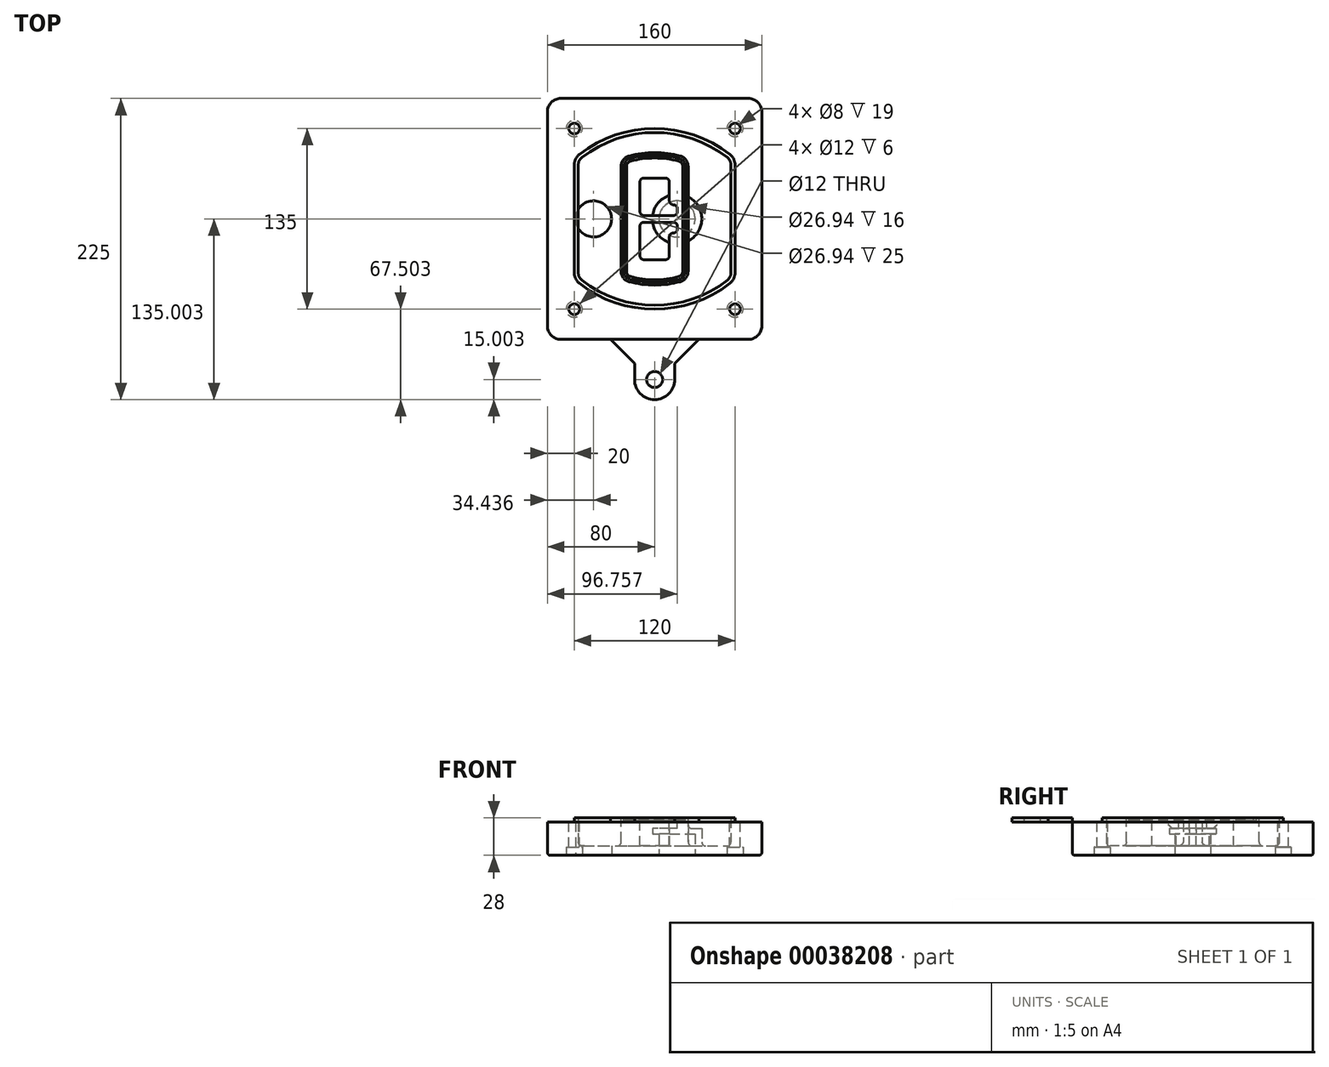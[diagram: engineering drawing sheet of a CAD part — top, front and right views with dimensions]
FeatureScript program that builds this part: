
annotation { "Feature Type Name" : "Feature", "Feature Type Description" : "" }
export const myFeature = defineFeature(function(context is Context, id is Id, definition is map)
    precondition{}
    {
        {
            var Q0;
            Q0=qCreatedBy(makeId("Top.planeOp"),FACE);
            var sketch = newSketch(context, id + "F0", { "sketchPlane" : qUnion([Q0])});
            skPoint(sketch, "E0.rect.middle", {"position": v(0, 0) * mm});
            skLineSegment(sketch, "E1.bottom", {"start": v(24.05, 28.38) * mm, "end": v(164.05, 28.38) * mm});
            skLineSegment(sketch, "E1.top", {"start": v(24.05, 208.38) * mm, "end": v(164.05, 208.38) * mm});
            skLineSegment(sketch, "E1.left", {"start": v(14.05, 38.38) * mm, "end": v(14.05, 198.38) * mm});
            skLineSegment(sketch, "E1.right", {"start": v(174.05, 38.38) * mm, "end": v(174.05, 198.38) * mm});
            skLineSegment(sketch, "E2", {"start": v(14.05, 208.38) * mm, "end": v(174.05, 28.38) * mm, "construction": true});
            skLineSegment(sketch, "E3", {"start": v(174.05, 208.38) * mm, "end": v(14.05, 28.38) * mm, "construction": true});
            skCircle(sketch, "E4", {"center": v(34.05, 185.88) * mm, "radius": 4 * mm});
            skCircle(sketch, "E5", {"center": v(154.05, 185.88) * mm, "radius": 4 * mm});
            skCircle(sketch, "E6", {"center": v(154.05, 50.88) * mm, "radius": 4 * mm});
            skCircle(sketch, "E7", {"center": v(34.05, 50.88) * mm, "radius": 4 * mm});
            skLineSegment(sketch, "E8", {"start": v(34.05, 185.88) * mm, "end": v(154.05, 185.88) * mm, "construction": true});
            skLineSegment(sketch, "E9", {"start": v(154.05, 185.88) * mm, "end": v(154.05, 50.88) * mm, "construction": true});
            skLineSegment(sketch, "E10", {"start": v(154.05, 50.88) * mm, "end": v(34.05, 50.88) * mm, "construction": true});
            skLineSegment(sketch, "E11", {"start": v(34.05, 50.88) * mm, "end": v(34.05, 185.88) * mm, "construction": true});
            skLineSegment(sketch, "E12", {"start": v(34.05, 158.68) * mm, "end": v(34.05, 78.09) * mm});
            skLineSegment(sketch, "E13", {"start": v(154.05, 158.68) * mm, "end": v(154.05, 78.09) * mm});
            skArc(sketch, "E14", {"start": v(150.2, 166.56) * mm, "mid": v(94.05, 185.88) * mm, "end": v(37.9, 166.56) * mm});
            skArc(sketch, "E15", {"start": v(37.9, 70.2) * mm, "mid": v(94.05, 50.88) * mm, "end": v(150.2, 70.2) * mm});
            skLineSegment(sketch, "E16", {"start": v(34.05, 118.38) * mm, "end": v(154.05, 118.38) * mm, "construction": true});
            skPoint(sketch, "E17.visualSharp", {"position": v(34.05, 73.38) * mm});
            skArc(sketch, "E17.filletArc", {"start": v(34.05, 78.09) * mm, "mid": v(35.06, 73.7) * mm, "end": v(37.9, 70.2) * mm});
            skPoint(sketch, "E18.visualSharp", {"position": v(34.05, 163.38) * mm});
            skArc(sketch, "E18.filletArc", {"start": v(37.9, 166.56) * mm, "mid": v(35.06, 163.06) * mm, "end": v(34.05, 158.68) * mm});
            skPoint(sketch, "E19.visualSharp", {"position": v(154.05, 163.38) * mm});
            skArc(sketch, "E19.filletArc", {"start": v(154.05, 158.68) * mm, "mid": v(153.04, 163.06) * mm, "end": v(150.2, 166.56) * mm});
            skPoint(sketch, "E20.visualSharp", {"position": v(154.05, 73.38) * mm});
            skArc(sketch, "E20.filletArc", {"start": v(150.2, 70.2) * mm, "mid": v(153.04, 73.7) * mm, "end": v(154.05, 78.09) * mm});
            skPoint(sketch, "E21.visualSharp", {"position": v(14.05, 208.38) * mm});
            skArc(sketch, "E21.filletArc", {"start": v(24.05, 208.38) * mm, "mid": v(16.98, 205.45) * mm, "end": v(14.05, 198.38) * mm});
            skPoint(sketch, "E22.visualSharp", {"position": v(174.05, 208.38) * mm});
            skArc(sketch, "E22.filletArc", {"start": v(174.05, 198.38) * mm, "mid": v(171.12, 205.45) * mm, "end": v(164.05, 208.38) * mm});
            skPoint(sketch, "E23.visualSharp", {"position": v(174.05, 28.38) * mm});
            skArc(sketch, "E23.filletArc", {"start": v(164.05, 28.38) * mm, "mid": v(171.12, 31.31) * mm, "end": v(174.05, 38.38) * mm});
            skPoint(sketch, "E24.visualSharp", {"position": v(14.05, 28.38) * mm});
            skArc(sketch, "E24.filletArc", {"start": v(14.05, 38.38) * mm, "mid": v(16.98, 31.31) * mm, "end": v(24.05, 28.38) * mm});
            skArc(sketch, "E25.0", {"start": v(151.05, 158.68) * mm, "mid": v(150.34, 161.75) * mm, "end": v(148.36, 164.2) * mm});
            skLineSegment(sketch, "E25.1", {"start": v(151.05, 158.68) * mm, "end": v(151.05, 78.09) * mm});
            skArc(sketch, "E25.2", {"start": v(148.36, 72.57) * mm, "mid": v(150.34, 75.02) * mm, "end": v(151.05, 78.09) * mm});
            skArc(sketch, "E25.3", {"start": v(39.74, 72.57) * mm, "mid": v(94.05, 53.88) * mm, "end": v(148.36, 72.57) * mm});
            skArc(sketch, "E25.4", {"start": v(37.05, 78.09) * mm, "mid": v(37.76, 75.02) * mm, "end": v(39.74, 72.57) * mm});
            skArc(sketch, "E25.5", {"start": v(148.36, 164.2) * mm, "mid": v(94.05, 182.88) * mm, "end": v(39.74, 164.2) * mm});
            skLineSegment(sketch, "E25.6", {"start": v(37.05, 158.68) * mm, "end": v(37.05, 78.09) * mm});
            skArc(sketch, "E25.7", {"start": v(39.74, 164.2) * mm, "mid": v(37.76, 161.75) * mm, "end": v(37.05, 158.68) * mm});
            skArc(sketch, "E26.0", {"start": v(35.43, 169.71) * mm, "mid": v(31.47, 164.82) * mm, "end": v(30.05, 158.68) * mm});
            skArc(sketch, "E26.1", {"start": v(152.67, 169.71) * mm, "mid": v(94.05, 189.88) * mm, "end": v(35.43, 169.71) * mm});
            skArc(sketch, "E26.2", {"start": v(158.05, 158.68) * mm, "mid": v(156.63, 164.82) * mm, "end": v(152.67, 169.71) * mm});
            skLineSegment(sketch, "E26.3", {"start": v(158.05, 158.68) * mm, "end": v(158.05, 78.09) * mm});
            skArc(sketch, "E26.4", {"start": v(152.67, 67.05) * mm, "mid": v(156.63, 71.95) * mm, "end": v(158.05, 78.09) * mm});
            skLineSegment(sketch, "E26.5", {"start": v(30.05, 158.68) * mm, "end": v(30.05, 78.09) * mm});
            skArc(sketch, "E26.6", {"start": v(35.43, 67.05) * mm, "mid": v(94.05, 46.88) * mm, "end": v(152.67, 67.05) * mm});
            skArc(sketch, "E26.7", {"start": v(30.05, 78.09) * mm, "mid": v(31.47, 71.95) * mm, "end": v(35.43, 67.05) * mm});
            skSolve(sketch);
        }
        {
            var Q0;
            Q0=makeQuery(id+"F0.imprint","IMPRINT",FACE,{"disambiguationData":[TD([[makeQuery(id+"F0.imprint","IMPRINT",EDGE,{"derivedFrom":sQuery(id+"F0.wireOp",EDGE,"E1.bottom")}),1.0]])]});
            var Q1;
            Q1=makeQuery(id+"F0.imprint","IMPRINT",FACE,{"disambiguationData":[TD([[makeQuery(id+"F0.imprint","IMPRINT",EDGE,{"derivedFrom":sQuery(id+"F0.wireOp",EDGE,"E12")}),1.0]])]});
            var Q2;
            Q2=makeQuery(id+"F0.imprint","IMPRINT",FACE,{"disambiguationData":[TD([[makeQuery(id+"F0.imprint","IMPRINT",EDGE,{"derivedFrom":sQuery(id+"F0.wireOp",EDGE,"E25.0")}),1.0]])]});
            var Q3;
            Q3=makeQuery(id+"F0.imprint","IMPRINT",FACE,{"disambiguationData":[TD([[makeQuery(id+"F0.imprint","IMPRINT",EDGE,{"derivedFrom":sQuery(id+"F0.wireOp",EDGE,"E12")}),-1.0]])]});
            extrude(context, id + "F1", {"entities" : qUnion([Q0, Q1, Q2, Q3]), "oppositeDirection" : true, "depth" : 25 * mm});
        }
        {
            var Q0;
            Q0=makeQuery(id+"F0.imprint","IMPRINT",FACE,{"disambiguationData":[TD([[makeQuery(id+"F0.imprint","IMPRINT",EDGE,{"derivedFrom":sQuery(id+"F0.wireOp",EDGE,"E12")}),1.0]])]});
            extrude(context, id + "F2", {"entities" : qUnion([Q0]), "operationType" : NewBodyOperationType.ADD, "depth" : 3 * mm});
        }
        {
            var Q0;
            Q0=makeQuery(id+"F0.imprint","IMPRINT",FACE,{"disambiguationData":[TD([[makeQuery(id+"F0.imprint","IMPRINT",EDGE,{"derivedFrom":sQuery(id+"F0.wireOp",EDGE,"E25.0")}),1.0]])]});
            extrude(context, id + "F3", {"entities" : qUnion([Q0]), "operationType" : NewBodyOperationType.REMOVE, "oppositeDirection" : true, "depth" : 18 * mm});
        }
        {
            var Q0;
            Q0=makeQuery(id+"F2.opExtrude","CAP_FACE",FACE,{"disambiguationData":[OSD([sQuery(id+"F0.wireOp",EDGE,"E12"),sQuery(id+"F0.wireOp",EDGE,"E13"),sQuery(id+"F0.wireOp",EDGE,"E14"),sQuery(id+"F0.wireOp",EDGE,"E15"),sQuery(id+"F0.wireOp",EDGE,"E17.filletArc"),sQuery(id+"F0.wireOp",EDGE,"E18.filletArc"),sQuery(id+"F0.wireOp",EDGE,"E19.filletArc"),sQuery(id+"F0.wireOp",EDGE,"E20.filletArc"),sQuery(id+"F0.wireOp",EDGE,"E25.0"),sQuery(id+"F0.wireOp",EDGE,"E25.1"),sQuery(id+"F0.wireOp",EDGE,"E25.2"),sQuery(id+"F0.wireOp",EDGE,"E25.3"),sQuery(id+"F0.wireOp",EDGE,"E25.4"),sQuery(id+"F0.wireOp",EDGE,"E25.5"),sQuery(id+"F0.wireOp",EDGE,"E25.6"),sQuery(id+"F0.wireOp",EDGE,"E25.7")])],"isStart":false});
            var sketch = newSketch(context, id + "F4", { "sketchPlane" : qUnion([Q0])});
            skArc(sketch, "E27.0", {"start": v(74.97, 71.41) * mm, "mid": v(94.05, 68.88) * mm, "end": v(113.13, 71.41) * mm});
            skArc(sketch, "E28.0", {"start": v(113.13, 165.35) * mm, "mid": v(94.05, 167.88) * mm, "end": v(74.97, 165.35) * mm});
            skLineSegment(sketch, "E29", {"start": v(69.05, 157.63) * mm, "end": v(69.05, 79.14) * mm});
            skLineSegment(sketch, "E30", {"start": v(119.05, 157.63) * mm, "end": v(119.05, 79.14) * mm});
            skLineSegment(sketch, "E31", {"start": v(69.05, 163.48) * mm, "end": v(119.05, 163.48) * mm, "construction": true});
            skLineSegment(sketch, "E32", {"start": v(69.05, 73.28) * mm, "end": v(119.05, 73.28) * mm, "construction": true});
            skPoint(sketch, "E33.visualSharp", {"position": v(69.05, 163.48) * mm});
            skArc(sketch, "E33.filletArc", {"start": v(74.97, 165.35) * mm, "mid": v(70.7, 162.5) * mm, "end": v(69.05, 157.63) * mm});
            skPoint(sketch, "E34.visualSharp", {"position": v(119.05, 163.48) * mm});
            skArc(sketch, "E34.filletArc", {"start": v(119.05, 157.63) * mm, "mid": v(117.4, 162.5) * mm, "end": v(113.13, 165.35) * mm});
            skPoint(sketch, "E35.visualSharp", {"position": v(119.05, 73.28) * mm});
            skArc(sketch, "E35.filletArc", {"start": v(113.13, 71.41) * mm, "mid": v(117.4, 74.27) * mm, "end": v(119.05, 79.14) * mm});
            skPoint(sketch, "E36.visualSharp", {"position": v(69.05, 73.28) * mm});
            skArc(sketch, "E36.filletArc", {"start": v(69.05, 79.14) * mm, "mid": v(70.7, 74.27) * mm, "end": v(74.97, 71.41) * mm});
            skArc(sketch, "E37.0", {"start": v(148.36, 164.2) * mm, "mid": v(94.05, 182.88) * mm, "end": v(39.74, 164.2) * mm});
            skArc(sketch, "E37.1", {"start": v(39.74, 164.2) * mm, "mid": v(37.76, 161.75) * mm, "end": v(37.05, 158.68) * mm});
            skLineSegment(sketch, "E37.2", {"start": v(37.05, 158.68) * mm, "end": v(37.05, 78.09) * mm});
            skArc(sketch, "E37.3", {"start": v(37.05, 78.09) * mm, "mid": v(37.76, 75.02) * mm, "end": v(39.74, 72.57) * mm});
            skArc(sketch, "E37.4", {"start": v(39.74, 72.57) * mm, "mid": v(94.05, 53.88) * mm, "end": v(148.36, 72.57) * mm});
            skArc(sketch, "E37.5", {"start": v(148.36, 72.57) * mm, "mid": v(150.34, 75.02) * mm, "end": v(151.05, 78.09) * mm});
            skLineSegment(sketch, "E37.6", {"start": v(151.05, 158.68) * mm, "end": v(151.05, 78.09) * mm});
            skArc(sketch, "E37.7", {"start": v(151.05, 158.68) * mm, "mid": v(150.34, 161.75) * mm, "end": v(148.36, 164.2) * mm});
            skLineSegment(sketch, "E38.0", {"start": v(117.05, 157.63) * mm, "end": v(117.05, 79.14) * mm});
            skArc(sketch, "E38.1", {"start": v(112.61, 73.34) * mm, "mid": v(115.81, 75.49) * mm, "end": v(117.05, 79.14) * mm});
            skArc(sketch, "E38.2", {"start": v(75.49, 73.34) * mm, "mid": v(94.05, 70.88) * mm, "end": v(112.61, 73.34) * mm});
            skArc(sketch, "E38.3", {"start": v(71.05, 79.14) * mm, "mid": v(72.29, 75.49) * mm, "end": v(75.49, 73.34) * mm});
            skLineSegment(sketch, "E38.4", {"start": v(71.05, 157.63) * mm, "end": v(71.05, 79.14) * mm});
            skArc(sketch, "E38.5", {"start": v(117.05, 157.63) * mm, "mid": v(115.81, 161.28) * mm, "end": v(112.61, 163.42) * mm});
            skArc(sketch, "E38.6", {"start": v(75.49, 163.42) * mm, "mid": v(72.29, 161.28) * mm, "end": v(71.05, 157.63) * mm});
            skArc(sketch, "E38.7", {"start": v(112.61, 163.42) * mm, "mid": v(94.05, 165.88) * mm, "end": v(75.49, 163.42) * mm});
            skArc(sketch, "E39.0", {"start": v(115.05, 157.63) * mm, "mid": v(114.23, 160.06) * mm, "end": v(112.1, 161.5) * mm});
            skLineSegment(sketch, "E39.1", {"start": v(115.05, 157.63) * mm, "end": v(115.05, 79.14) * mm});
            skArc(sketch, "E39.2", {"start": v(112.1, 75.27) * mm, "mid": v(114.23, 76.7) * mm, "end": v(115.05, 79.14) * mm});
            skArc(sketch, "E39.3", {"start": v(76, 75.27) * mm, "mid": v(94.05, 72.88) * mm, "end": v(112.1, 75.27) * mm});
            skArc(sketch, "E39.4", {"start": v(73.05, 79.14) * mm, "mid": v(73.87, 76.7) * mm, "end": v(76, 75.27) * mm});
            skArc(sketch, "E39.5", {"start": v(112.1, 161.5) * mm, "mid": v(94.05, 163.88) * mm, "end": v(76, 161.5) * mm});
            skLineSegment(sketch, "E39.6", {"start": v(73.05, 157.63) * mm, "end": v(73.05, 79.14) * mm});
            skArc(sketch, "E39.7", {"start": v(76, 161.5) * mm, "mid": v(73.87, 160.06) * mm, "end": v(73.05, 157.63) * mm});
            skLineSegment(sketch, "E40", {"start": v(69.05, 118.38) * mm, "end": v(119.05, 118.38) * mm, "construction": true});
            skLineSegment(sketch, "E41", {"start": v(83.05, 123.88) * mm, "end": v(83.05, 145.88) * mm});
            skLineSegment(sketch, "E42", {"start": v(86.05, 148.88) * mm, "end": v(102.05, 148.88) * mm});
            skLineSegment(sketch, "E43", {"start": v(105.05, 145.88) * mm, "end": v(105.05, 131.88) * mm});
            skLineSegment(sketch, "E44", {"start": v(108.05, 128.88) * mm, "end": v(108.05, 128.88) * mm});
            skLineSegment(sketch, "E45", {"start": v(111.05, 125.88) * mm, "end": v(111.05, 123.88) * mm});
            skLineSegment(sketch, "E46", {"start": v(108.05, 120.88) * mm, "end": v(86.05, 120.88) * mm});
            skPoint(sketch, "E47.visualSharp", {"position": v(83.05, 148.88) * mm});
            skArc(sketch, "E47.filletArc", {"start": v(86.05, 148.88) * mm, "mid": v(83.93, 148) * mm, "end": v(83.05, 145.88) * mm});
            skPoint(sketch, "E48.visualSharp", {"position": v(105.05, 148.88) * mm});
            skArc(sketch, "E48.filletArc", {"start": v(105.05, 145.88) * mm, "mid": v(104.17, 148) * mm, "end": v(102.05, 148.88) * mm});
            skPoint(sketch, "E49.visualSharp", {"position": v(105.05, 128.88) * mm});
            skArc(sketch, "E49.filletArc", {"start": v(105.05, 131.88) * mm, "mid": v(105.93, 129.76) * mm, "end": v(108.05, 128.88) * mm});
            skPoint(sketch, "E50.visualSharp", {"position": v(111.05, 128.88) * mm});
            skArc(sketch, "E50.filletArc", {"start": v(111.05, 125.88) * mm, "mid": v(110.17, 128) * mm, "end": v(108.05, 128.88) * mm});
            skPoint(sketch, "E51.visualSharp", {"position": v(111.05, 120.88) * mm});
            skArc(sketch, "E51.filletArc", {"start": v(108.05, 120.88) * mm, "mid": v(110.17, 121.76) * mm, "end": v(111.05, 123.88) * mm});
            skPoint(sketch, "E52.visualSharp", {"position": v(83.05, 120.88) * mm});
            skArc(sketch, "E52.filletArc", {"start": v(83.05, 123.88) * mm, "mid": v(83.93, 121.76) * mm, "end": v(86.05, 120.88) * mm});
            skLineSegment(sketch, "E53.0.MirrorCS", {"start": v(108.05, 115.88) * mm, "end": v(86.05, 115.88) * mm});
            skArc(sketch, "E54.0.MirrorCS", {"start": v(83.05, 112.88) * mm, "mid": v(83.93, 115) * mm, "end": v(86.05, 115.88) * mm});
            skLineSegment(sketch, "E55.0.MirrorCS", {"start": v(83.05, 112.88) * mm, "end": v(83.05, 90.88) * mm});
            skArc(sketch, "E56.0.MirrorCS", {"start": v(86.05, 87.88) * mm, "mid": v(83.93, 88.76) * mm, "end": v(83.05, 90.88) * mm});
            skLineSegment(sketch, "E57.0.MirrorCS", {"start": v(86.05, 87.88) * mm, "end": v(102.05, 87.88) * mm});
            skArc(sketch, "E58.0.MirrorCS", {"start": v(105.05, 90.88) * mm, "mid": v(104.17, 88.76) * mm, "end": v(102.05, 87.88) * mm});
            skLineSegment(sketch, "E59.0.MirrorCS", {"start": v(105.05, 90.88) * mm, "end": v(105.05, 104.88) * mm});
            skArc(sketch, "E60.0.MirrorCS", {"start": v(105.05, 104.88) * mm, "mid": v(105.93, 107) * mm, "end": v(108.05, 107.88) * mm});
            skArc(sketch, "E61.0.MirrorCS", {"start": v(111.05, 110.88) * mm, "mid": v(110.17, 108.76) * mm, "end": v(108.05, 107.88) * mm});
            skLineSegment(sketch, "E62.0.MirrorCS", {"start": v(111.05, 110.88) * mm, "end": v(111.05, 112.88) * mm});
            skArc(sketch, "E63.0.MirrorCS", {"start": v(108.05, 115.88) * mm, "mid": v(110.17, 115) * mm, "end": v(111.05, 112.88) * mm});
            skSolve(sketch);
        }
        {
            var Q0;
            Q0=makeQuery(id+"F4.imprint","IMPRINT",FACE,{"disambiguationData":[TD([[makeQuery(id+"F4.imprint","IMPRINT",EDGE,{"derivedFrom":sQuery(id+"F4.wireOp",EDGE,"E27.0")}),1.0]])]});
            var Q1;
            Q1=makeQuery(id+"F4.imprint","IMPRINT",FACE,{"disambiguationData":[TD([[makeQuery(id+"F4.imprint","IMPRINT",EDGE,{"derivedFrom":sQuery(id+"F4.wireOp",EDGE,"E38.0")}),-1.0]])]});
            var Q2;
            Q2=makeQuery(id+"F4.imprint","IMPRINT",FACE,{"disambiguationData":[TD([[makeQuery(id+"F4.imprint","IMPRINT",EDGE,{"derivedFrom":sQuery(id+"F4.wireOp",EDGE,"E39.0")}),1.0]])]});
            extrude(context, id + "F5", {"entities" : qUnion([Q0, Q1, Q2]), "operationType" : NewBodyOperationType.ADD, "endBound" : BoundingType.UP_TO_NEXT, "oppositeDirection" : true, "depth" : 25 * mm});
        }
        {
            var Q0;
            Q0=makeQuery(id+"F4.imprint","IMPRINT",FACE,{"disambiguationData":[TD([[makeQuery(id+"F4.imprint","IMPRINT",EDGE,{"derivedFrom":sQuery(id+"F4.wireOp",EDGE,"E38.0")}),-1.0]])]});
            extrude(context, id + "F6", {"entities" : qUnion([Q0]), "operationType" : NewBodyOperationType.REMOVE, "oppositeDirection" : true, "depth" : 2 * mm});
        }
        {
            var Q0;
            Q0=makeQuery(id+"F1.opExtrude","CAP_FACE",FACE,{"disambiguationData":[OSD([sQuery(id+"F0.wireOp",EDGE,"E1.bottom"),sQuery(id+"F0.wireOp",EDGE,"E1.top"),sQuery(id+"F0.wireOp",EDGE,"E1.left"),sQuery(id+"F0.wireOp",EDGE,"E1.right"),sQuery(id+"F0.wireOp",EDGE,"E4"),sQuery(id+"F0.wireOp",EDGE,"E5"),sQuery(id+"F0.wireOp",EDGE,"E6"),sQuery(id+"F0.wireOp",EDGE,"E7"),sQuery(id+"F0.wireOp",EDGE,"E21.filletArc"),sQuery(id+"F0.wireOp",EDGE,"E22.filletArc"),sQuery(id+"F0.wireOp",EDGE,"E23.filletArc"),sQuery(id+"F0.wireOp",EDGE,"E24.filletArc")])],"isStart":false});
            var sketch = newSketch(context, id + "F7", { "sketchPlane" : qUnion([Q0])});
            skCircle(sketch, "E64", {"center": v(110.8, -118.38) * mm, "radius": 13.47 * mm});
            skCircle(sketch, "E65", {"center": v(48.49, -118.38) * mm, "radius": 13.47 * mm});
            skLineSegment(sketch, "E66", {"start": v(174.05, -118.38) * mm, "end": v(14.05, -118.38) * mm});
            skCircle(sketch, "E67", {"center": v(110.8, -118.38) * mm, "radius": 18.47 * mm});
            skCircle(sketch, "E68", {"center": v(154.05, -185.88) * mm, "radius": 6 * mm});
            skCircle(sketch, "E69", {"center": v(34.05, -185.88) * mm, "radius": 6 * mm});
            skCircle(sketch, "E70", {"center": v(34.05, -50.88) * mm, "radius": 6 * mm});
            skCircle(sketch, "E71", {"center": v(154.05, -50.88) * mm, "radius": 6 * mm});
            skSolve(sketch);
        }
        {
            var Q0;
            {var subQ1=sQuery(id+"F7.wireOp",EDGE,"E66");var subQ4=sQuery(id+"F7.wireOp",EDGE,"E64");var subQ6=makeQuery(id+"F7.imprint","INTERSECT",VERTEX,{"disambiguationData":[OD(0.0)],"derivedFrom":[subQ4,subQ1]});Q0=makeQuery(id+"F7.imprint","IMPRINT",FACE,{"disambiguationData":[TD([[makeQuery(id+"F7.imprint","IMPRINT",EDGE,{"disambiguationData":[TD([[subQ6,-1.0]])],"derivedFrom":subQ4}),-1.0]])]});}
            var Q1;
            {var subQ0=sQuery(id+"F7.wireOp",EDGE,"E66");var subQ1=sQuery(id+"F7.wireOp",EDGE,"E64");var subQ3=makeQuery(id+"F7.imprint","INTERSECT",VERTEX,{"disambiguationData":[OD(0.0)],"derivedFrom":[subQ1,subQ0]});Q1=makeQuery(id+"F7.imprint","IMPRINT",FACE,{"disambiguationData":[TD([[makeQuery(id+"F7.imprint","IMPRINT",EDGE,{"disambiguationData":[TD([[subQ3,-1.0]])],"derivedFrom":subQ1}),1.0]])]});}
            var Q2;
            {var subQ0=sQuery(id+"F7.wireOp",EDGE,"E66");var subQ1=sQuery(id+"F7.wireOp",EDGE,"E64");var subQ3=makeQuery(id+"F7.imprint","INTERSECT",VERTEX,{"disambiguationData":[OD(0.0)],"derivedFrom":[subQ1,subQ0]});Q2=makeQuery(id+"F7.imprint","IMPRINT",FACE,{"disambiguationData":[TD([[makeQuery(id+"F7.imprint","IMPRINT",EDGE,{"disambiguationData":[TD([[subQ3,1.0]])],"derivedFrom":subQ1}),1.0]])]});}
            var Q3;
            {var subQ1=sQuery(id+"F7.wireOp",EDGE,"E66");var subQ4=sQuery(id+"F7.wireOp",EDGE,"E64");var subQ6=makeQuery(id+"F7.imprint","INTERSECT",VERTEX,{"disambiguationData":[OD(0.0)],"derivedFrom":[subQ4,subQ1]});Q3=makeQuery(id+"F7.imprint","IMPRINT",FACE,{"disambiguationData":[TD([[makeQuery(id+"F7.imprint","IMPRINT",EDGE,{"disambiguationData":[TD([[subQ6,1.0]])],"derivedFrom":subQ4}),-1.0]])]});}
            extrude(context, id + "F8", {"entities" : qUnion([Q0, Q1, Q2, Q3]), "operationType" : NewBodyOperationType.ADD, "oppositeDirection" : true, "depth" : 20 * mm});
        }
        {
            var Q0;
            {var subQ0=sQuery(id+"F7.wireOp",EDGE,"E66");var subQ1=sQuery(id+"F7.wireOp",EDGE,"E64");var subQ3=makeQuery(id+"F7.imprint","INTERSECT",VERTEX,{"disambiguationData":[OD(0.0)],"derivedFrom":[subQ1,subQ0]});Q0=makeQuery(id+"F7.imprint","IMPRINT",FACE,{"disambiguationData":[TD([[makeQuery(id+"F7.imprint","IMPRINT",EDGE,{"disambiguationData":[TD([[subQ3,-1.0]])],"derivedFrom":subQ1}),1.0]])]});}
            var Q1;
            {var subQ0=sQuery(id+"F7.wireOp",EDGE,"E66");var subQ1=sQuery(id+"F7.wireOp",EDGE,"E64");var subQ3=makeQuery(id+"F7.imprint","INTERSECT",VERTEX,{"disambiguationData":[OD(0.0)],"derivedFrom":[subQ1,subQ0]});Q1=makeQuery(id+"F7.imprint","IMPRINT",FACE,{"disambiguationData":[TD([[makeQuery(id+"F7.imprint","IMPRINT",EDGE,{"disambiguationData":[TD([[subQ3,1.0]])],"derivedFrom":subQ1}),1.0]])]});}
            extrude(context, id + "F9", {"entities" : qUnion([Q0, Q1]), "operationType" : NewBodyOperationType.REMOVE, "oppositeDirection" : true, "depth" : 16 * mm});
        }
        {
            var Q0;
            {var subQ0=sQuery(id+"F7.wireOp",EDGE,"E66");var subQ1=sQuery(id+"F7.wireOp",EDGE,"E65");var subQ3=makeQuery(id+"F7.imprint","INTERSECT",VERTEX,{"disambiguationData":[OD(0.0)],"derivedFrom":[subQ1,subQ0]});Q0=makeQuery(id+"F7.imprint","IMPRINT",FACE,{"disambiguationData":[TD([[makeQuery(id+"F7.imprint","IMPRINT",EDGE,{"disambiguationData":[TD([[subQ3,-1.0]])],"derivedFrom":subQ1}),1.0]])]});}
            var Q1;
            {var subQ0=sQuery(id+"F7.wireOp",EDGE,"E66");var subQ1=sQuery(id+"F7.wireOp",EDGE,"E65");var subQ3=makeQuery(id+"F7.imprint","INTERSECT",VERTEX,{"disambiguationData":[OD(0.0)],"derivedFrom":[subQ1,subQ0]});Q1=makeQuery(id+"F7.imprint","IMPRINT",FACE,{"disambiguationData":[TD([[makeQuery(id+"F7.imprint","IMPRINT",EDGE,{"disambiguationData":[TD([[subQ3,1.0]])],"derivedFrom":subQ1}),1.0]])]});}
            extrude(context, id + "F10", {"entities" : qUnion([Q0, Q1]), "operationType" : NewBodyOperationType.REMOVE, "oppositeDirection" : true, "depth" : 25 * mm});
        }
        {
            var Q0;
            Q0=makeQuery(id+"F7.imprint","IMPRINT",FACE,{"disambiguationData":[TD([[makeQuery(id+"F7.imprint","IMPRINT",EDGE,{"derivedFrom":sQuery(id+"F7.wireOp",EDGE,"E68")}),1.0]])]});
            var Q1;
            Q1=makeQuery(id+"F7.imprint","IMPRINT",FACE,{"disambiguationData":[TD([[makeQuery(id+"F7.imprint","IMPRINT",EDGE,{"derivedFrom":makeQuery(id+"F1.opExtrude","CAP_EDGE",EDGE,{"disambiguationData":[OSD([sQuery(id+"F0.wireOp",EDGE,"E5")])],"isStart":false})}),-1.0]])]});
            var Q2;
            Q2=makeQuery(id+"F7.imprint","IMPRINT",FACE,{"disambiguationData":[TD([[makeQuery(id+"F7.imprint","IMPRINT",EDGE,{"derivedFrom":sQuery(id+"F7.wireOp",EDGE,"E69")}),1.0]])]});
            var Q3;
            Q3=makeQuery(id+"F7.imprint","IMPRINT",FACE,{"disambiguationData":[TD([[makeQuery(id+"F7.imprint","IMPRINT",EDGE,{"derivedFrom":makeQuery(id+"F1.opExtrude","CAP_EDGE",EDGE,{"disambiguationData":[OSD([sQuery(id+"F0.wireOp",EDGE,"E4")])],"isStart":false})}),-1.0]])]});
            var Q4;
            Q4=makeQuery(id+"F7.imprint","IMPRINT",FACE,{"disambiguationData":[TD([[makeQuery(id+"F7.imprint","IMPRINT",EDGE,{"derivedFrom":sQuery(id+"F7.wireOp",EDGE,"E70")}),1.0]])]});
            var Q5;
            Q5=makeQuery(id+"F7.imprint","IMPRINT",FACE,{"disambiguationData":[TD([[makeQuery(id+"F7.imprint","IMPRINT",EDGE,{"derivedFrom":makeQuery(id+"F1.opExtrude","CAP_EDGE",EDGE,{"disambiguationData":[OSD([sQuery(id+"F0.wireOp",EDGE,"E7")])],"isStart":false})}),-1.0]])]});
            var Q6;
            Q6=makeQuery(id+"F7.imprint","IMPRINT",FACE,{"disambiguationData":[TD([[makeQuery(id+"F7.imprint","IMPRINT",EDGE,{"derivedFrom":sQuery(id+"F7.wireOp",EDGE,"E71")}),1.0]])]});
            var Q7;
            Q7=makeQuery(id+"F7.imprint","IMPRINT",FACE,{"disambiguationData":[TD([[makeQuery(id+"F7.imprint","IMPRINT",EDGE,{"derivedFrom":makeQuery(id+"F1.opExtrude","CAP_EDGE",EDGE,{"disambiguationData":[OSD([sQuery(id+"F0.wireOp",EDGE,"E6")])],"isStart":false})}),-1.0]])]});
            extrude(context, id + "F11", {"entities" : qUnion([Q0, Q1, Q2, Q3, Q4, Q5, Q6, Q7]), "operationType" : NewBodyOperationType.REMOVE, "oppositeDirection" : true, "depth" : 6 * mm});
        }
        {
            var Q0;
            Q0=makeQuery(id+"F9.boolean.opBoolean","COPY",FACE,{"derivedFrom":makeQuery(id+"F9.opExtrude","CAP_FACE",FACE,{"disambiguationData":[OSD([sQuery(id+"F7.wireOp",EDGE,"E64")])],"isStart":false})});
            var sketch = newSketch(context, id + "F12", { "sketchPlane" : qUnion([Q0])});
            skArc(sketch, "E72.0", {"start": v(105.05, -100.83) * mm, "mid": v(96.62, -106.56) * mm, "end": v(92.5, -115.88) * mm});
            skArc(sketch, "E72.1", {"start": v(92.5, -120.88) * mm, "mid": v(96.62, -130.2) * mm, "end": v(105.05, -135.93) * mm});
            skLineSegment(sketch, "E73", {"start": v(92.5, -120.88) * mm, "end": v(108.05, -120.88) * mm});
            skLineSegment(sketch, "E74.0", {"start": v(108.05, -115.88) * mm, "end": v(92.5, -115.88) * mm});
            skArc(sketch, "E74.1", {"start": v(108.05, -115.88) * mm, "mid": v(110.17, -115) * mm, "end": v(111.05, -112.88) * mm});
            skLineSegment(sketch, "E74.2", {"start": v(111.05, -110.88) * mm, "end": v(111.05, -112.88) * mm});
            skArc(sketch, "E74.3", {"start": v(111.05, -110.88) * mm, "mid": v(110.17, -108.76) * mm, "end": v(108.05, -107.88) * mm});
            skArc(sketch, "E74.4", {"start": v(105.05, -104.88) * mm, "mid": v(105.93, -107) * mm, "end": v(108.05, -107.88) * mm});
            skLineSegment(sketch, "E74.5", {"start": v(105.05, -100.83) * mm, "end": v(105.05, -104.88) * mm});
            skLineSegment(sketch, "E74.7", {"start": v(108.05, -120.88) * mm, "end": v(92.5, -120.88) * mm});
            skArc(sketch, "E74.8", {"start": v(108.05, -120.88) * mm, "mid": v(110.17, -121.76) * mm, "end": v(111.05, -123.88) * mm});
            skLineSegment(sketch, "E74.9", {"start": v(111.05, -125.88) * mm, "end": v(111.05, -123.88) * mm});
            skArc(sketch, "E74.10", {"start": v(111.05, -125.88) * mm, "mid": v(110.17, -128) * mm, "end": v(108.05, -128.88) * mm});
            skArc(sketch, "E74.11", {"start": v(105.05, -131.88) * mm, "mid": v(105.93, -129.76) * mm, "end": v(108.05, -128.88) * mm});
            skLineSegment(sketch, "E74.12", {"start": v(105.05, -135.93) * mm, "end": v(105.05, -131.88) * mm});
            skPoint(sketch, "E75.orphan", {"position": v(105.05, -145.88) * mm});
            skPoint(sketch, "E76.orphan", {"position": v(86.05, -120.88) * mm});
            skPoint(sketch, "E77.orphan", {"position": v(86.05, -115.88) * mm});
            skPoint(sketch, "E78.orphan", {"position": v(105.05, -90.88) * mm});
            skSolve(sketch);
        }
        {
            var Q0;
            {var subQ7=sQuery(id+"F12.wireOp",EDGE,"E72.0");var subQ14=sQuery(id+"F12.wireOp",EDGE,"E72.1");var subQ16=sQuery(id+"F12.wireOp",EDGE,"E74.1");var subQ18=sQuery(id+"F12.wireOp",EDGE,"E74.8");Q0=qUnion([makeQuery(id+"F12.imprint","IMPRINT",FACE,{"disambiguationData":[TD([[makeQuery(id+"F12.imprint","IMPRINT",EDGE,{"derivedFrom":subQ7}),1.0]])]}),makeQuery(id+"F12.imprint","IMPRINT",FACE,{"disambiguationData":[TD([[makeQuery(id+"F12.imprint","IMPRINT",EDGE,{"derivedFrom":subQ14}),1.0]])]}),makeQuery(id+"F12.imprint","IMPRINT",FACE,{"disambiguationData":[TD([[makeQuery(id+"F12.imprint","IMPRINT",EDGE,{"derivedFrom":subQ16}),1.0]])]}),makeQuery(id+"F12.imprint","IMPRINT",FACE,{"disambiguationData":[TD([[makeQuery(id+"F12.imprint","IMPRINT",EDGE,{"derivedFrom":subQ18}),-1.0]])]})]);}
            var Q1;
            Q1=makeQuery(id+"F5.boolean.opBoolean","SPLIT",FACE,{"disambiguationData":[TD([makeQuery(id+"F5.opExtrude","SWEPT_FACE",FACE,{"disambiguationData":[OSD([sQuery(id+"F4.wireOp",EDGE,"E41")])]})])],"derivedFrom":makeQuery(id+"F3.boolean.opBoolean","COPY",FACE,{"derivedFrom":makeQuery(id+"F3.opExtrude","CAP_FACE",FACE,{"disambiguationData":[OSD([sQuery(id+"F0.wireOp",EDGE,"E25.0"),sQuery(id+"F0.wireOp",EDGE,"E25.1"),sQuery(id+"F0.wireOp",EDGE,"E25.2"),sQuery(id+"F0.wireOp",EDGE,"E25.3"),sQuery(id+"F0.wireOp",EDGE,"E25.4"),sQuery(id+"F0.wireOp",EDGE,"E25.5"),sQuery(id+"F0.wireOp",EDGE,"E25.6"),sQuery(id+"F0.wireOp",EDGE,"E25.7")])],"isStart":false})})});
            extrude(context, id + "F13", {"entities" : qUnion([Q0]), "operationType" : NewBodyOperationType.REMOVE, "endBound" : BoundingType.UP_TO_SURFACE, "endBoundEntityFace" : qUnion([Q1]), "depth" : 25 * mm});
        }
        {
            var Q0;
            Q0=makeQuery(id+"F3.boolean.opBoolean","COPY",EDGE,{"derivedFrom":makeQuery(id+"F3.opExtrude","CAP_EDGE",EDGE,{"disambiguationData":[OSD([sQuery(id+"F0.wireOp",EDGE,"E25.6")])],"isStart":false})});
            var Q1;
            Q1=makeQuery(id+"F8.boolean.opBoolean","INTERSECT",EDGE,{"derivedFrom":[makeQuery(id+"F5.opExtrude","SWEPT_FACE",FACE,{"disambiguationData":[OSD([sQuery(id+"F4.wireOp",EDGE,"E30")])]}),makeQuery(id+"F8.opExtrude","CAP_FACE",FACE,{"disambiguationData":[OSD([sQuery(id+"F7.wireOp",EDGE,"E67")])],"isStart":false})]});
            var Q2;
            Q2=makeQuery(id+"F8.boolean.opBoolean","INTERSECT",EDGE,{"disambiguationData":[OD(1.0)],"derivedFrom":[makeQuery(id+"F5.opExtrude","SWEPT_FACE",FACE,{"disambiguationData":[OSD([sQuery(id+"F4.wireOp",EDGE,"E30")])]}),makeQuery(id+"F8.opExtrude","SWEPT_FACE",FACE,{"disambiguationData":[OSD([sQuery(id+"F7.wireOp",EDGE,"E67")])]})]});
            var Q3;
            {var subQ0=sQuery(id+"F4.wireOp",EDGE,"E30");Q3=makeQuery(id+"F8.boolean.opBoolean","SPLIT",EDGE,{"disambiguationData":[TD([makeQuery(id+"F5.opExtrude","SWEPT_FACE",FACE,{"disambiguationData":[OSD([sQuery(id+"F4.wireOp",EDGE,"E35.filletArc")])]})])],"derivedFrom":makeQuery(id+"F5.opExtrude","CAP_EDGE",EDGE,{"disambiguationData":[OSD([subQ0])],"isStart":false})});}
            var Q4;
            {var subQ0=sQuery(id+"F0.wireOp",EDGE,"E25.7");var subQ1=sQuery(id+"F0.wireOp",EDGE,"E25.1");var subQ2=sQuery(id+"F0.wireOp",EDGE,"E25.6");var subQ3=sQuery(id+"F0.wireOp",EDGE,"E25.5");var subQ4=sQuery(id+"F0.wireOp",EDGE,"E25.4");var subQ5=sQuery(id+"F0.wireOp",EDGE,"E25.0");var subQ6=sQuery(id+"F0.wireOp",EDGE,"E25.2");var subQ7=sQuery(id+"F0.wireOp",EDGE,"E25.3");Q4=makeQuery(id+"F8.boolean.opBoolean","INTERSECT",EDGE,{"derivedFrom":[makeQuery(id+"F5.boolean.opBoolean","SPLIT",FACE,{"disambiguationData":[TD([makeQuery(id+"F2.opExtrude","SWEPT_FACE",FACE,{"disambiguationData":[OSD([subQ5])]})])],"derivedFrom":makeQuery(id+"F3.boolean.opBoolean","COPY",FACE,{"derivedFrom":makeQuery(id+"F3.opExtrude","CAP_FACE",FACE,{"disambiguationData":[OSD([subQ5,subQ1,subQ6,subQ7,subQ4,subQ3,subQ2,subQ0])],"isStart":false})})}),makeQuery(id+"F8.opExtrude","SWEPT_FACE",FACE,{"disambiguationData":[OSD([sQuery(id+"F7.wireOp",EDGE,"E67")])]})]});}
            var Q5;
            Q5=makeQuery(id+"F8.boolean.opBoolean","INTERSECT",EDGE,{"disambiguationData":[OD(0.0)],"derivedFrom":[makeQuery(id+"F5.opExtrude","SWEPT_FACE",FACE,{"disambiguationData":[OSD([sQuery(id+"F4.wireOp",EDGE,"E30")])]}),makeQuery(id+"F8.opExtrude","SWEPT_FACE",FACE,{"disambiguationData":[OSD([sQuery(id+"F7.wireOp",EDGE,"E67")])]})]});
            fillet(context, id + "F14", {"entities" : qUnion([Q0, Q1, Q2, Q3, Q4, Q5]), "radius" : 3 * mm, "tangentPropagation" : true, "allowEdgeOverflow" : false});
        }
        {
            var Q0;
            Q0=makeQuery(id+"F1.opExtrude","CAP_EDGE",EDGE,{"disambiguationData":[OSD([sQuery(id+"F0.wireOp",EDGE,"E1.bottom")])],"isStart":false});
            fillet(context, id + "F15", {"entities" : qUnion([Q0]), "radius" : 2 * mm, "tangentPropagation" : true, "allowEdgeOverflow" : false});
        }
        {
            var Q0;
            {var subQ0=sQuery(id+"F0.wireOp",EDGE,"E1.bottom");var subQ1=sQuery(id+"F0.wireOp",EDGE,"E1.top");var subQ2=sQuery(id+"F0.wireOp",EDGE,"E1.left");var subQ3=sQuery(id+"F0.wireOp",EDGE,"E1.right");var subQ4=sQuery(id+"F0.wireOp",EDGE,"E4");var subQ5=sQuery(id+"F0.wireOp",EDGE,"E5");var subQ6=sQuery(id+"F0.wireOp",EDGE,"E6");var subQ7=sQuery(id+"F0.wireOp",EDGE,"E7");var subQ8=sQuery(id+"F0.wireOp",EDGE,"E21.filletArc");var subQ9=sQuery(id+"F0.wireOp",EDGE,"E22.filletArc");var subQ10=sQuery(id+"F0.wireOp",EDGE,"E23.filletArc");var subQ11=sQuery(id+"F0.wireOp",EDGE,"E24.filletArc");Q0=makeQuery(id+"F2.boolean.opBoolean","SPLIT",FACE,{"disambiguationData":[TD([makeQuery(id+"F1.opExtrude","SWEPT_FACE",FACE,{"disambiguationData":[OSD([subQ0])]})])],"derivedFrom":makeQuery(id+"F1.opExtrude","CAP_FACE",FACE,{"disambiguationData":[OSD([subQ0,subQ1,subQ2,subQ3,subQ4,subQ5,subQ6,subQ7,subQ8,subQ9,subQ10,subQ11])],"isStart":true})});}
            var sketch = newSketch(context, id + "F16", { "sketchPlane" : qUnion([Q0])});
            skLineSegment(sketch, "E79.0", {"start": v(24.05, 208.38) * mm, "end": v(164.05, 208.38) * mm});
            skArc(sketch, "E79.1", {"start": v(24.05, 208.38) * mm, "mid": v(16.98, 205.45) * mm, "end": v(14.05, 198.38) * mm});
            skLineSegment(sketch, "E79.2", {"start": v(14.05, 38.38) * mm, "end": v(14.05, 198.38) * mm});
            skArc(sketch, "E79.3", {"start": v(14.05, 38.38) * mm, "mid": v(16.98, 31.31) * mm, "end": v(24.05, 28.38) * mm});
            skLineSegment(sketch, "E79.4", {"start": v(24.05, 28.38) * mm, "end": v(164.05, 28.38) * mm});
            skArc(sketch, "E79.5", {"start": v(164.05, 28.38) * mm, "mid": v(171.12, 31.31) * mm, "end": v(174.05, 38.38) * mm});
            skLineSegment(sketch, "E79.6", {"start": v(174.05, 38.38) * mm, "end": v(174.05, 198.38) * mm});
            skArc(sketch, "E79.7", {"start": v(174.05, 198.38) * mm, "mid": v(171.12, 205.45) * mm, "end": v(164.05, 208.38) * mm});
            skCircle(sketch, "E79.8", {"center": v(154.05, 185.88) * mm, "radius": 4 * mm});
            skCircle(sketch, "E79.9", {"center": v(34.05, 185.88) * mm, "radius": 4 * mm});
            skArc(sketch, "E79.10", {"start": v(150.2, 166.56) * mm, "mid": v(94.05, 185.88) * mm, "end": v(37.9, 166.56) * mm});
            skArc(sketch, "E79.11", {"start": v(37.9, 166.56) * mm, "mid": v(35.06, 163.06) * mm, "end": v(34.05, 158.68) * mm});
            skLineSegment(sketch, "E79.12", {"start": v(34.05, 158.68) * mm, "end": v(34.05, 78.09) * mm});
            skArc(sketch, "E79.13", {"start": v(154.05, 158.68) * mm, "mid": v(153.04, 163.06) * mm, "end": v(150.2, 166.56) * mm});
            skLineSegment(sketch, "E79.14", {"start": v(154.05, 158.68) * mm, "end": v(154.05, 78.09) * mm});
            skArc(sketch, "E79.15", {"start": v(150.2, 70.2) * mm, "mid": v(153.04, 73.7) * mm, "end": v(154.05, 78.09) * mm});
            skArc(sketch, "E79.16", {"start": v(37.9, 70.2) * mm, "mid": v(94.05, 50.88) * mm, "end": v(150.2, 70.2) * mm});
            skCircle(sketch, "E79.17", {"center": v(154.05, 50.88) * mm, "radius": 4 * mm});
            skCircle(sketch, "E79.18", {"center": v(34.05, 50.88) * mm, "radius": 4 * mm});
            skArc(sketch, "E79.19", {"start": v(34.05, 78.09) * mm, "mid": v(35.06, 73.7) * mm, "end": v(37.9, 70.2) * mm});
            skArc(sketch, "E80.1", {"start": v(24.05, 188.38) * mm, "mid": v(31.12, 205.45) * mm, "end": v(14.05, 198.38) * mm});
            skLineSegment(sketch, "E81", {"start": v(94.05, 208.38) * mm, "end": v(94.05, 238.38) * mm, "construction": true});
            skLineSegment(sketch, "E82", {"start": v(79.05, 238.38) * mm, "end": v(79.05, 226.38) * mm});
            skLineSegment(sketch, "E83", {"start": v(109.05, 226.38) * mm, "end": v(109.05, 238.38) * mm});
            skArc(sketch, "E84", {"start": v(109.05, 238.38) * mm, "mid": v(94.05, 253.38) * mm, "end": v(79.05, 238.38) * mm});
            skCircle(sketch, "E85", {"center": v(94.05, 238.38) * mm, "radius": 6 * mm});
            skLineSegment(sketch, "E86", {"start": v(61.05, 208.38) * mm, "end": v(79.05, 226.38) * mm});
            skLineSegment(sketch, "E87", {"start": v(109.05, 226.38) * mm, "end": v(127.05, 208.38) * mm});
            skLineSegment(sketch, "E88", {"start": v(14.05, 118.38) * mm, "end": v(174.05, 118.38) * mm, "construction": true});
            skLineSegment(sketch, "E89.MirrorCS", {"start": v(79.05, 226.38) * mm, "end": v(61.05, 208.38) * mm});
            skLineSegment(sketch, "E90.MirrorCS", {"start": v(79.05, 226.38) * mm, "end": v(79.05, 238.38) * mm});
            skArc(sketch, "E91.MirrorCS", {"start": v(79.05, 238.38) * mm, "mid": v(94.05, 253.38) * mm, "end": v(109.05, 238.38) * mm});
            skLineSegment(sketch, "E92.MirrorCS", {"start": v(109.05, 238.38) * mm, "end": v(109.05, 226.38) * mm});
            skLineSegment(sketch, "E93.MirrorCS", {"start": v(127.05, 208.38) * mm, "end": v(109.05, 226.38) * mm});
            skLineSegment(sketch, "E94.MirrorCS", {"start": v(174.05, 118.38) * mm, "end": v(14.05, 118.38) * mm, "construction": true});
            skLineSegment(sketch, "E95.MirrorCS", {"start": v(164.05, 28.38) * mm, "end": v(24.05, 28.38) * mm});
            skCircle(sketch, "E96.MirrorC", {"center": v(94.05, -1.62) * mm, "radius": 6 * mm});
            skLineSegment(sketch, "E97.MirrorCS", {"start": v(79.05, -1.62) * mm, "end": v(79.05, 10.38) * mm});
            skLineSegment(sketch, "E98.MirrorCS", {"start": v(79.05, 10.38) * mm, "end": v(79.05, -1.62) * mm});
            skLineSegment(sketch, "E99.MirrorCS", {"start": v(61.05, 28.38) * mm, "end": v(79.05, 10.38) * mm});
            skLineSegment(sketch, "E100.MirrorCS", {"start": v(109.05, 10.38) * mm, "end": v(109.05, -1.62) * mm});
            skLineSegment(sketch, "E101.MirrorCS", {"start": v(79.05, 10.38) * mm, "end": v(61.05, 28.38) * mm});
            skLineSegment(sketch, "E102.MirrorCS", {"start": v(109.05, -1.62) * mm, "end": v(109.05, 10.38) * mm});
            skLineSegment(sketch, "E103.MirrorCS", {"start": v(127.05, 28.38) * mm, "end": v(109.05, 10.38) * mm});
            skArc(sketch, "E104.MirrorCS", {"start": v(109.05, -1.62) * mm, "mid": v(94.05, -16.62) * mm, "end": v(79.05, -1.62) * mm});
            skArc(sketch, "E105.MirrorCS", {"start": v(79.05, -1.62) * mm, "mid": v(94.05, -16.62) * mm, "end": v(109.05, -1.62) * mm});
            skLineSegment(sketch, "E106.MirrorCS", {"start": v(109.05, 10.38) * mm, "end": v(127.05, 28.38) * mm});
            skArc(sketch, "E107.MirrorCS", {"start": v(174.05, 38.38) * mm, "mid": v(171.12, 31.31) * mm, "end": v(164.05, 28.38) * mm});
            skArc(sketch, "E108.MirrorCS", {"start": v(154.05, 78.09) * mm, "mid": v(153.04, 73.7) * mm, "end": v(150.2, 70.2) * mm});
            skLineSegment(sketch, "E109.MirrorCS", {"start": v(94.05, 28.38) * mm, "end": v(94.05, -1.62) * mm});
            skSolve(sketch);
        }
        {
            var Q0;
            Q0=makeQuery(id+"F16.imprint","IMPRINT",FACE,{"disambiguationData":[TD([[makeQuery(id+"F16.imprint","IMPRINT",EDGE,{"derivedFrom":sQuery(id+"F16.wireOp",EDGE,"E91.MirrorCS")}),-1.0]])]});
            var Q1;
            {var subQ3=sQuery(id+"F16.wireOp",EDGE,"E99.MirrorCS");Q1=makeQuery(id+"F16.imprint","IMPRINT",FACE,{"disambiguationData":[TD([[makeQuery(id+"F16.imprint","IMPRINT",EDGE,{"derivedFrom":subQ3}),1.0]])]});}
            var Q2;
            {var subQ5=sQuery(id+"F16.wireOp",EDGE,"E80.1");Q2=makeQuery(id+"F16.imprint","IMPRINT",FACE,{"disambiguationData":[TD([[makeQuery(id+"F16.imprint","IMPRINT",EDGE,{"derivedFrom":subQ5}),1.0]])]});}
            var Q3;
            {var subQ0=sQuery(id+"F4.wireOp",EDGE,"E36.filletArc");var subQ1=sQuery(id+"F4.wireOp",EDGE,"E35.filletArc");var subQ2=sQuery(id+"F4.wireOp",EDGE,"E34.filletArc");var subQ3=sQuery(id+"F4.wireOp",EDGE,"E33.filletArc");var subQ4=sQuery(id+"F4.wireOp",EDGE,"E27.0");var subQ5=sQuery(id+"F4.wireOp",EDGE,"E30");var subQ6=sQuery(id+"F4.wireOp",EDGE,"E28.0");var subQ7=sQuery(id+"F4.wireOp",EDGE,"E29");Q3=makeQuery(id+"F6.boolean.opBoolean","SPLIT",FACE,{"disambiguationData":[TD([makeQuery(id+"F5.opExtrude","SWEPT_FACE",FACE,{"disambiguationData":[OSD([subQ4])]})])],"derivedFrom":makeQuery(id+"F5.opExtrude","CAP_FACE",FACE,{"disambiguationData":[OSD([subQ4,subQ6,subQ7,subQ5,subQ3,subQ2,subQ1,subQ0,sQuery(id+"F4.wireOp",EDGE,"E41"),sQuery(id+"F4.wireOp",EDGE,"E42"),sQuery(id+"F4.wireOp",EDGE,"E43"),sQuery(id+"F4.wireOp",EDGE,"E45"),sQuery(id+"F4.wireOp",EDGE,"E46"),sQuery(id+"F4.wireOp",EDGE,"E47.filletArc"),sQuery(id+"F4.wireOp",EDGE,"E48.filletArc"),sQuery(id+"F4.wireOp",EDGE,"E49.filletArc"),sQuery(id+"F4.wireOp",EDGE,"E50.filletArc"),sQuery(id+"F4.wireOp",EDGE,"E51.filletArc"),sQuery(id+"F4.wireOp",EDGE,"E52.filletArc"),sQuery(id+"F4.wireOp",EDGE,"E53.0.MirrorCS"),sQuery(id+"F4.wireOp",EDGE,"E54.0.MirrorCS"),sQuery(id+"F4.wireOp",EDGE,"E55.0.MirrorCS"),sQuery(id+"F4.wireOp",EDGE,"E56.0.MirrorCS"),sQuery(id+"F4.wireOp",EDGE,"E57.0.MirrorCS"),sQuery(id+"F4.wireOp",EDGE,"E58.0.MirrorCS"),sQuery(id+"F4.wireOp",EDGE,"E59.0.MirrorCS"),sQuery(id+"F4.wireOp",EDGE,"E60.0.MirrorCS"),sQuery(id+"F4.wireOp",EDGE,"E61.0.MirrorCS"),sQuery(id+"F4.wireOp",EDGE,"E62.0.MirrorCS"),sQuery(id+"F4.wireOp",EDGE,"E63.0.MirrorCS")])],"isStart":true})});}
            extrude(context, id + "F17", {"entities" : qUnion([Q0, Q1, Q2]), "operationType" : NewBodyOperationType.ADD, "endBound" : BoundingType.UP_TO_SURFACE, "endBoundEntityFace" : qUnion([Q3]), "depth" : 25 * mm});
        }
    });
